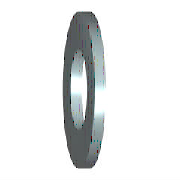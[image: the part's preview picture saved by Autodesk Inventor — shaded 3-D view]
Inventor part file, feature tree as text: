
AUTODESK INVENTOR PART (.ipt)
format: ipt  version: 2024.1 (Build 281209000, 209)  size: 105,472 bytes
history: native  units: mm (DEFAULTED — no unit token found)
features: other x1, plane x1
ambient origin geometry x7: Origin, YZ Plane, XY Plane, X Axis, Y Axis, Z Axis, Center Point
bodies: Solid1 (feature_tree), Body (feature_tree)
feature tree (2):
  other  "Work Axis1"
  plane  "Work Plane1"
